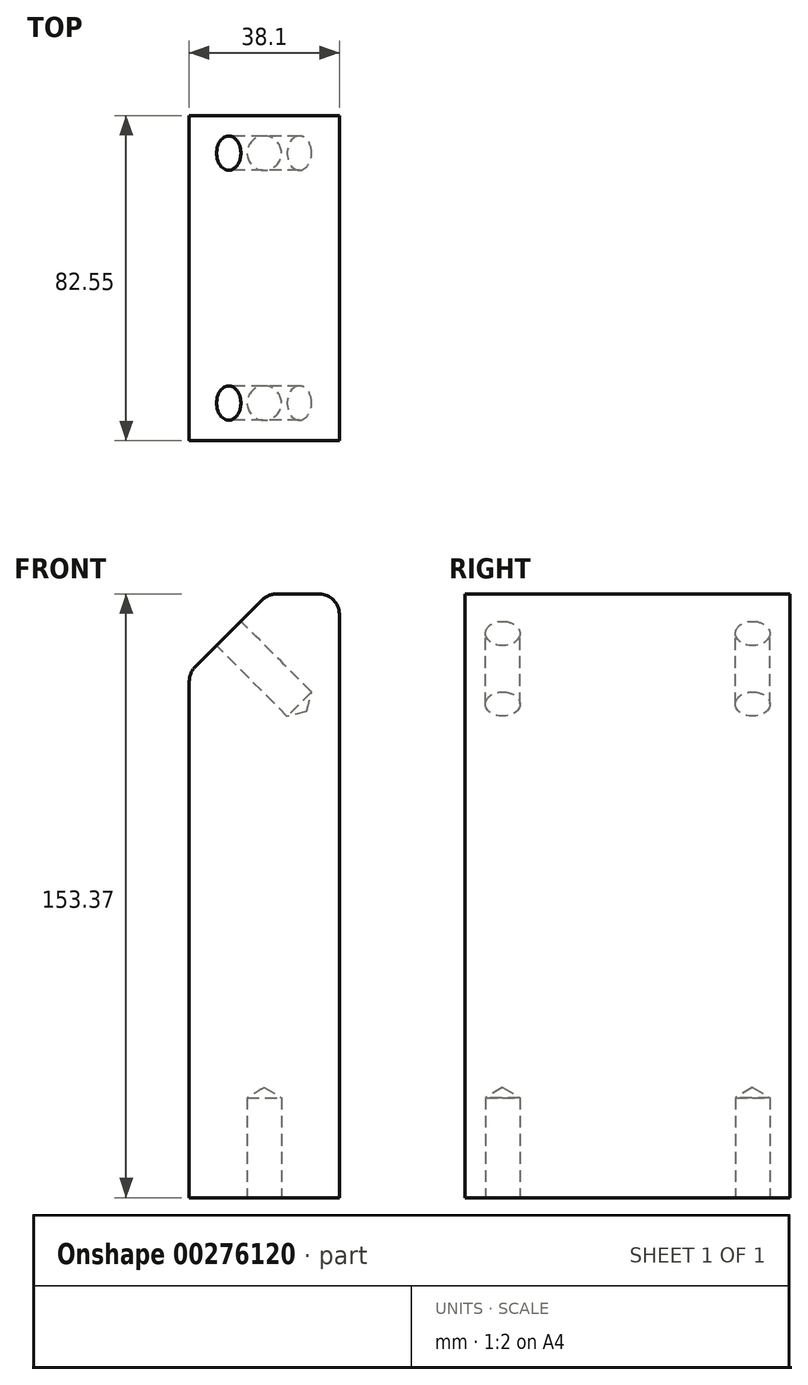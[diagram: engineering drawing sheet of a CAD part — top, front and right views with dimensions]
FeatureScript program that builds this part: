
annotation { "Feature Type Name" : "Feature", "Feature Type Description" : "" }
export const myFeature = defineFeature(function(context is Context, id is Id, definition is map)
    precondition{}
    {
        {
            var Q0;
            Q0=qCreatedBy(makeId("Front.planeOp"),FACE);
            var sketch = newSketch(context, id + "F0", { "sketchPlane" : qUnion([Q0])});
            skLineSegment(sketch, "E0", {"start": v(0, 0) * mm, "end": v(0, 153.37) * mm});
            skLineSegment(sketch, "E1", {"start": v(0, 153.37) * mm, "end": v(-18.08, 153.37) * mm});
            skLineSegment(sketch, "E2", {"start": v(-18.08, 153.37) * mm, "end": v(-38.1, 133.35) * mm});
            skLineSegment(sketch, "E3", {"start": v(-38.1, 133.35) * mm, "end": v(-38.1, 0) * mm});
            skLineSegment(sketch, "E4", {"start": v(-38.1, 0) * mm, "end": v(0, 0) * mm});
            skSolve(sketch);
        }
        {
            var Q0;
            Q0 = qSketchRegion(id + "F0", true);
            extrude(context, id + "F1", {"entities" : qUnion([Q0]), "depth" : 82.55 * mm});
        }
        {
            var Q0;
            Q0=makeQuery(id+"F1.opExtrude","SWEPT_FACE",FACE,{"disambiguationData":[OSD([sQuery(id+"F0.wireOp",EDGE,"E2")])]});
            var sketch = newSketch(context, id + "F2", { "sketchPlane" : qUnion([Q0])});
            skLineSegment(sketch, "E5", {"start": v(41.28, 95.66) * mm, "end": v(41.28, 67.35) * mm, "construction": true});
            skPoint(sketch, "E6", {"position": v(73.03, 81.5) * mm});
            skPoint(sketch, "E6.positionSnap0", {"position": v(82.55, 81.5) * mm});
            skPoint(sketch, "E7.MirrorP", {"position": v(9.53, 81.5) * mm});
            skSolve(sketch);
        }
        {
            var Q0;
            Q0=makeQuery(id+"F1.opExtrude","SWEPT_FACE",FACE,{"disambiguationData":[OSD([sQuery(id+"F0.wireOp",EDGE,"E4")])]});
            var sketch = newSketch(context, id + "F3", { "sketchPlane" : qUnion([Q0])});
            skLineSegment(sketch, "E8", {"start": v(-38.1, 41.28) * mm, "end": v(0, 41.28) * mm, "construction": true});
            skPoint(sketch, "E9", {"position": v(-19.05, 73.03) * mm});
            skPoint(sketch, "E9.positionSnap0", {"position": v(-19.05, 82.55) * mm});
            skPoint(sketch, "E10.MirrorP", {"position": v(-19.05, 9.53) * mm});
            skSolve(sketch);
        }
        {
            var Q0;
            Q0=sQuery(id+"F2.wireOp",VERTEX,"E6");
            var Q1;
            Q1=sQuery(id+"F2.wireOp",VERTEX,"E7.MirrorP");
            var Q2;
            Q2=sQuery(id+"F3.wireOp",VERTEX,"E9");
            var Q3;
            Q3=sQuery(id+"F3.wireOp",VERTEX,"E10.MirrorP");
            var Q4;
            Q4=makeQuery(id+"F1.opExtrude","SWEPT_BODY",BODY,{"disambiguationData":[OSD([sQuery(id+"F0.wireOp",EDGE,"E0"),sQuery(id+"F0.wireOp",EDGE,"E1"),sQuery(id+"F0.wireOp",EDGE,"E2"),sQuery(id+"F0.wireOp",EDGE,"E3"),sQuery(id+"F0.wireOp",EDGE,"E4")])]});
            hole(context, id + "F4", {"style" : HoleStyle.SIMPLE, "endStyle" : HoleEndStyle.BLIND, "holeDiameter" : 8.73 * mm, "holeDepth" : 25.4 * mm, "tappedDepth" : 12.7 * mm, "tapClearance" : 3, "locations" : qUnion([Q0, Q1, Q2, Q3]), "scope" : qUnion([Q4])});
        }
        {
            var Q0;
            Q0=makeQuery(id+"F1.opExtrude","SWEPT_EDGE",EDGE,{"disambiguationData":[OSD([sQuery(id+"F0.wireOp",EDGE,"E2"),sQuery(id+"F0.wireOp",EDGE,"E3")])]});
            var Q1;
            Q1=makeQuery(id+"F1.opExtrude","SWEPT_EDGE",EDGE,{"disambiguationData":[OSD([sQuery(id+"F0.wireOp",EDGE,"E1"),sQuery(id+"F0.wireOp",EDGE,"E2")])]});
            var Q2;
            Q2=makeQuery(id+"F1.opExtrude","SWEPT_EDGE",EDGE,{"disambiguationData":[OSD([sQuery(id+"F0.wireOp",EDGE,"E0"),sQuery(id+"F0.wireOp",EDGE,"E1")])]});
            fillet(context, id + "F5", {"entities" : qUnion([Q0, Q1, Q2]), "radius" : 5.08 * mm, "tangentPropagation" : true, "allowEdgeOverflow" : false});
        }
    });
